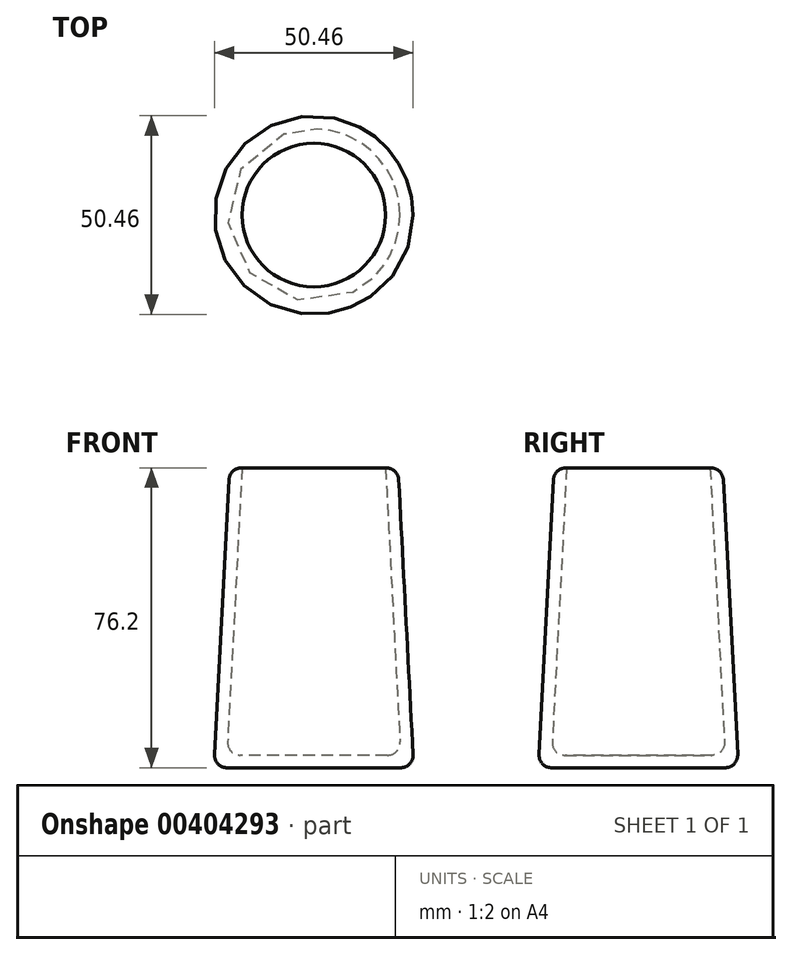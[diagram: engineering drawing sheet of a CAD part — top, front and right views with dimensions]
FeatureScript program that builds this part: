
annotation { "Feature Type Name" : "Feature", "Feature Type Description" : "" }
export const myFeature = defineFeature(function(context is Context, id is Id, definition is map)
    precondition{}
    {
        {
            var Q0;
            Q0=qCreatedBy(makeId("Top.planeOp"),FACE);
            var sketch = newSketch(context, id + "F0", { "sketchPlane" : qUnion([Q0])});
            skCircle(sketch, "E0", {"center": v(0, 0) * mm, "radius": 25.4 * mm});
            skSolve(sketch);
        }
        {
            var Q0;
            Q0=makeQuery(id+"F0.imprint","IMPRINT",FACE,{"disambiguationData":[TD([[makeQuery(id+"F0.imprint","IMPRINT",EDGE,{"derivedFrom":sQuery(id+"F0.wireOp",EDGE,"E0")}),1.0]])]});
            extrude(context, id + "F1", {"entities" : qUnion([Q0]), "depth" : 76.2 * mm, "hasDraft" : true, "draftAngle" : 3 * degree, "draftPullDirection" : true});
        }
        {
            var Q0;
            Q0=makeQuery(id+"F1.opExtrude","CAP_FACE",FACE,{"disambiguationData":[OSD([sQuery(id+"F0.wireOp",EDGE,"E0")])],"isStart":false});
            shell(context, id + "F2", {"entities" : qUnion([Q0]), "thickness" : 3.17 * mm});
        }
        {
            var Q0;
            {var subQ0=sQuery(id+"F0.wireOp",EDGE,"E0");Q0=makeQuery(id+"F2.opShell","OFFSET_EDGE",EDGE,{"disambiguationData":[OSD([subQ0]),TDD([makeQuery(id+"F1.opExtrude","CAP_EDGE",EDGE,{"disambiguationData":[OSD([subQ0])],"isStart":true})])]});}
            var Q1;
            Q1=makeQuery(id+"F1.opExtrude","CAP_EDGE",EDGE,{"disambiguationData":[OSD([sQuery(id+"F0.wireOp",EDGE,"E0")])],"isStart":false});
            var Q2;
            Q2=makeQuery(id+"F1.opExtrude","CAP_EDGE",EDGE,{"disambiguationData":[OSD([sQuery(id+"F0.wireOp",EDGE,"E0")])],"isStart":true});
            fillet(context, id + "F3", {"entities" : qUnion([Q0, Q1, Q2]), "radius" : 3.17 * mm, "tangentPropagation" : true, "allowEdgeOverflow" : false});
        }
    });
